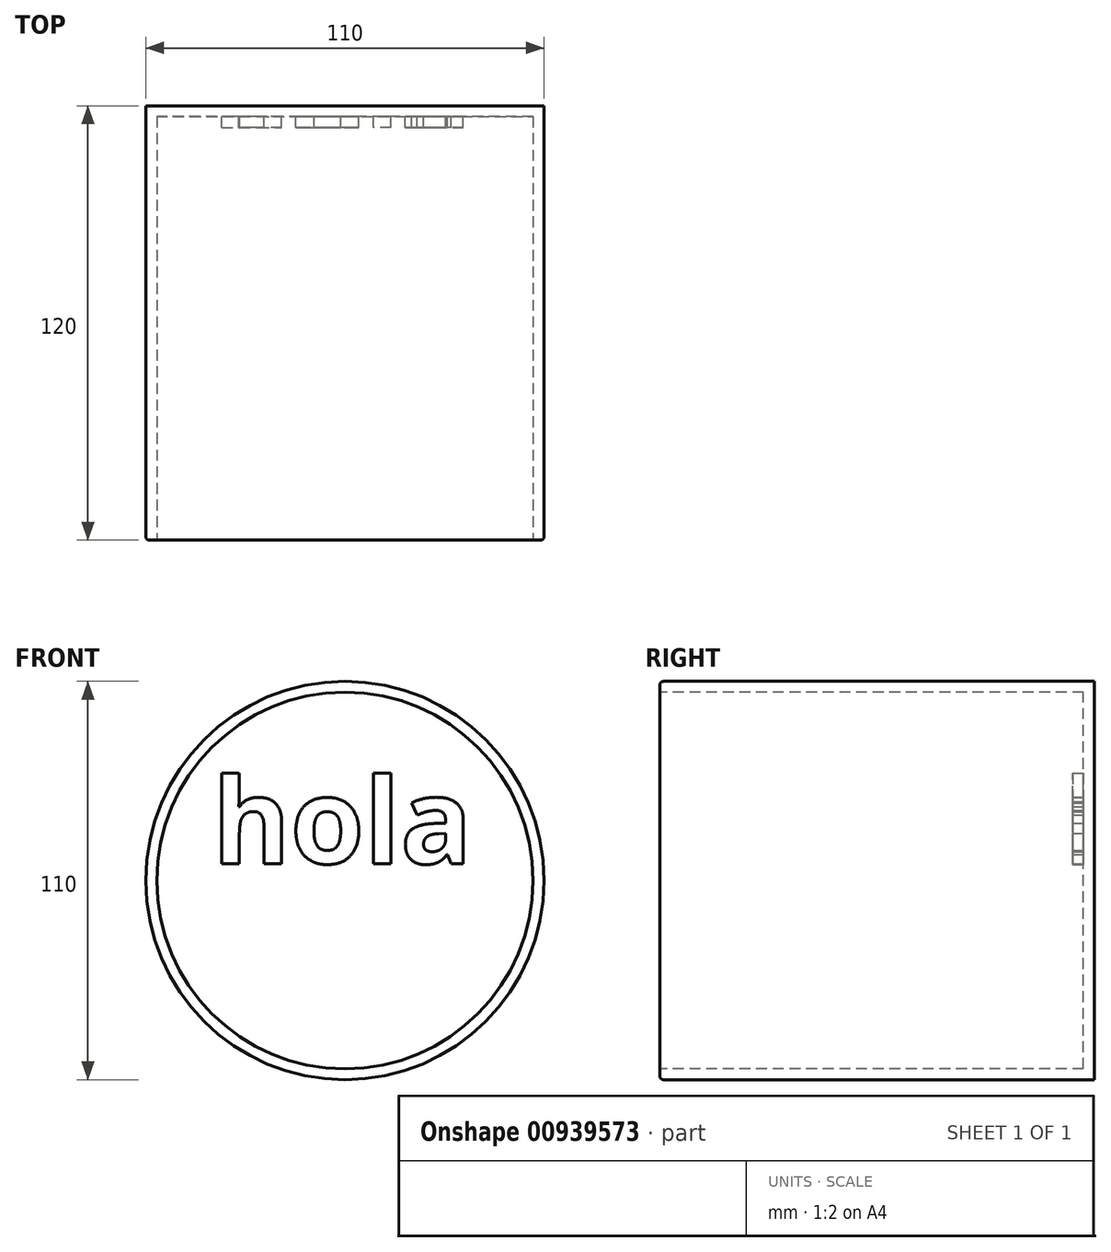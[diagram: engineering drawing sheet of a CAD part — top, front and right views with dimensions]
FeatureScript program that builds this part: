
annotation { "Feature Type Name" : "Feature", "Feature Type Description" : "" }
export const myFeature = defineFeature(function(context is Context, id is Id, definition is map)
    precondition{}
    {
        {
            var Q0;
            Q0=qCreatedBy(makeId("Front.planeOp"),FACE);
            var sketch = newSketch(context, id + "F0", { "sketchPlane" : qUnion([Q0])});
            skCircle(sketch, "E0", {"center": v(0, 0) * mm, "radius": 55 * mm});
            skSolve(sketch);
        }
        {
            var Q0;
            Q0=makeQuery(id+"F0.imprint","IMPRINT",FACE,{"disambiguationData":[TD([[makeQuery(id+"F0.imprint","IMPRINT",EDGE,{"derivedFrom":sQuery(id+"F0.wireOp",EDGE,"E0")}),1.0]])]});
            extrude(context, id + "F1", {"entities" : qUnion([Q0]), "depth" : 120 * mm, "offsetDistance" : 25 * mm});
        }
        {
            var Q0;
            Q0=makeQuery(id+"F1.opExtrude","CAP_FACE",FACE,{"disambiguationData":[OSD([sQuery(id+"F0.wireOp",EDGE,"E0")])],"isStart":false});
            var sketch = newSketch(context, id + "F2", { "sketchPlane" : qUnion([Q0])});
            skCircle(sketch, "E1", {"center": v(0, 0) * mm, "radius": 52 * mm});
            skSolve(sketch);
        }
        {
            var Q0;
            Q0=makeQuery(id+"F2.imprint","IMPRINT",FACE,{"disambiguationData":[TD([[makeQuery(id+"F2.imprint","IMPRINT",EDGE,{"derivedFrom":sQuery(id+"F2.wireOp",EDGE,"E1")}),1.0]])]});
            extrude(context, id + "F3", {"entities" : qUnion([Q0]), "operationType" : NewBodyOperationType.REMOVE, "oppositeDirection" : true, "depth" : 117 * mm, "offsetDistance" : 25 * mm});
        }
        {
            var Q0;
            Q0=makeQuery(id+"F3.boolean.opBoolean","COPY",EDGE,{"derivedFrom":makeQuery(id+"F3.opExtrude","CAP_EDGE",EDGE,{"disambiguationData":[OSD([sQuery(id+"F2.wireOp",EDGE,"E1")])],"isStart":true})});
            var Q1;
            Q1=makeQuery(id+"F1.opExtrude","CAP_EDGE",EDGE,{"disambiguationData":[OSD([sQuery(id+"F0.wireOp",EDGE,"E0")])],"isStart":false});
            fillet(context, id + "F4", {"entities" : qUnion([Q0, Q1]), "radius" : 1 * mm, "tangentPropagation" : true, "allowEdgeOverflow" : false});
        }
        {
            var Q0;
            Q0=makeQuery(id+"F3.boolean.opBoolean","COPY",FACE,{"derivedFrom":makeQuery(id+"F3.opExtrude","CAP_FACE",FACE,{"disambiguationData":[OSD([sQuery(id+"F2.wireOp",EDGE,"E1")])],"isStart":false})});
            var sketch = newSketch(context, id + "F5", { "sketchPlane" : qUnion([Q0])});
            skText(sketch, "E2", { "text": "hola", "fontName": "NotoSans-Bold.ttf"});
            const initialGuessF5  = {"E2": [-0.0366, 0.0047, 1, 0, 0.02364]};
            skSetInitialGuess(sketch, initialGuessF5);
            skSolve(sketch);
        }
        {
            var Q0;
            Q0 = qSketchRegion(id + "F5", true);
            extrude(context, id + "F6", {"entities" : qUnion([Q0]), "operationType" : NewBodyOperationType.ADD, "depth" : 3 * mm, "offsetDistance" : 25 * mm});
        }
    });
